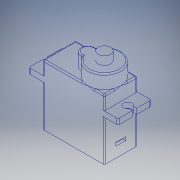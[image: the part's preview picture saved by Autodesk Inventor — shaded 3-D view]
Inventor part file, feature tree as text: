
AUTODESK INVENTOR PART (.ipt)
format: ipt  version: 2016 (Build 200138000, 138)  size: 278,528 bytes
history: native  units: mm
features: sketch x6, extrude x5, other x2, fillet x1
ambient origin geometry x8: Origin, YZ Plane, XZ Plane, XY Plane, X Axis, Y Axis, Z Axis, Center Point
bodies: Body1 (feature_tree)
feature tree (14):
  other  "솔리드1"
  extrude  "돌출1"  Depth=12.0mm
  other  "작업 평면1"
  extrude  "돌출2"  Depth=22.0mm TaperAngle=0.0deg
  extrude  "돌출3"  [1 undecoded]
  fillet  "모깎기1"  Radius=5.0mm
  extrude  "돌출4"  Depth=5.0mm
  extrude  "돌출6"  Depth=3.0mm
  sketch  "Sketch7"  dims[d0=22.5mm d1=12.0mm d2=22.0mm d3=0.0mm d4=-15.0mm d5=5.0mm d6=5.0mm d7=3.0mm d8=2.5mm d9=1.5mm d10=2.0mm d11=0.0mm d12=6.0mm d13=5.0mm d14=5.0mm d15=0.0mm d16=0.5mm d17=4.5mm d18=3.0mm d19=0.0mm d25=1.2mm d26=3.6mm d27=5.0mm d28=1.0mm d29=0.0mm d30=6.0mm]
  sketch  "스케치1"
  sketch  "스케치2"
  sketch  "스케치3"
  sketch  "스케치4"
  sketch  "스케치6"
note: 1 required parameter value undecoded (feature->parameter linkage not recoverable at this tier; creation-order binding heuristic only, values carry confidence <= 0.55)
